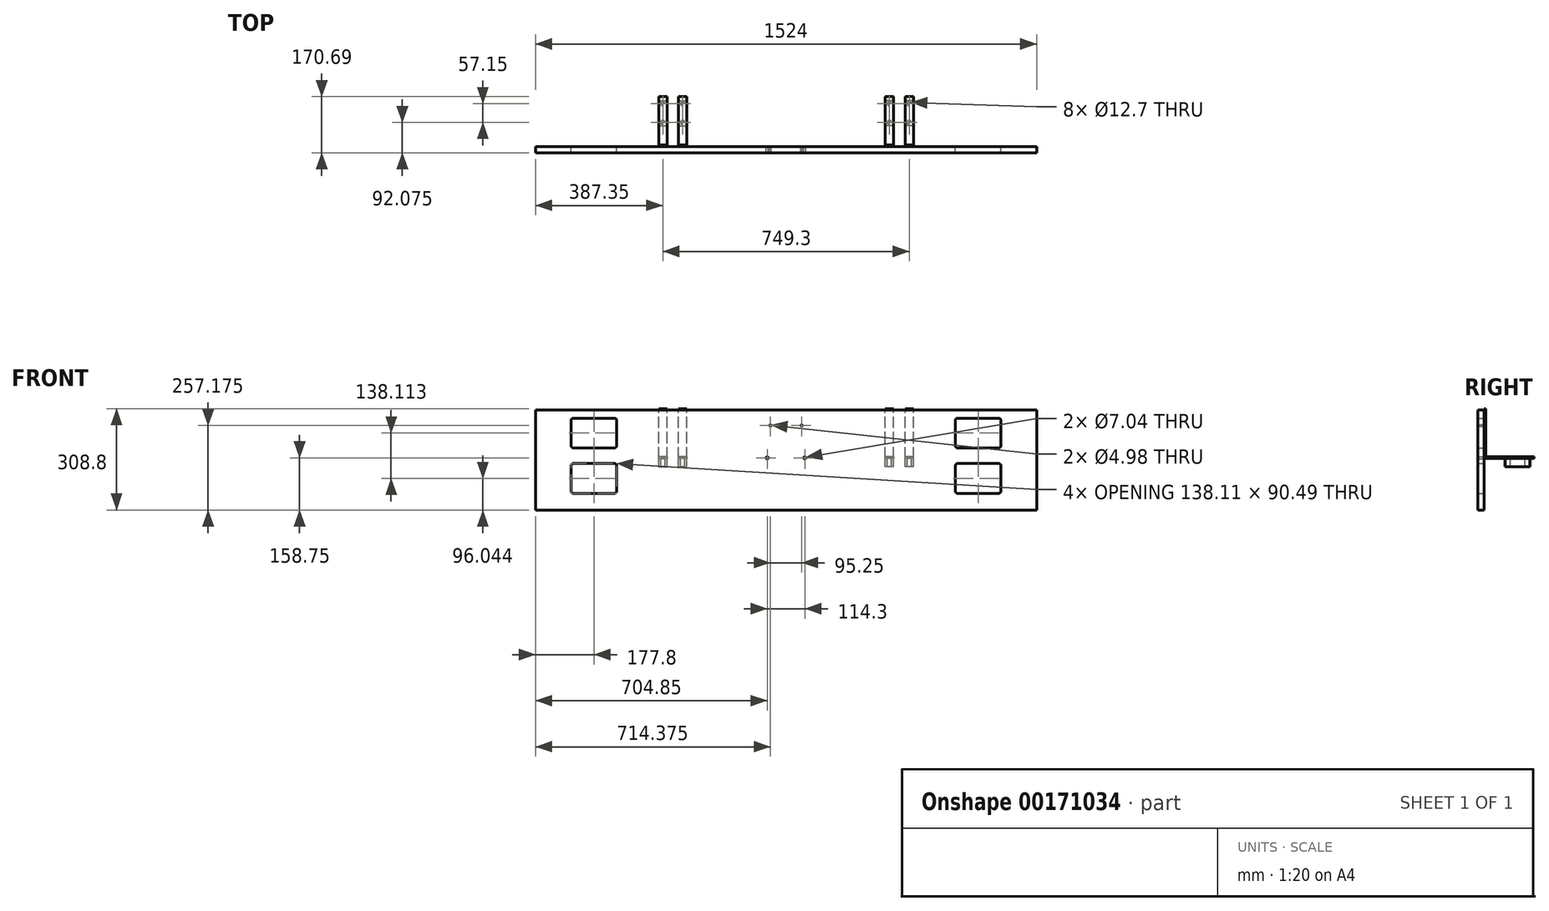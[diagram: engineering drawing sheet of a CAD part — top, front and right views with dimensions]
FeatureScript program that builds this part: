
annotation { "Feature Type Name" : "Feature", "Feature Type Description" : "" }
export const myFeature = defineFeature(function(context is Context, id is Id, definition is map)
    precondition{}
    {
        {
            var Q0;
            Q0=qCreatedBy(makeId("Front.planeOp"),FACE);
            var sketch = newSketch(context, id + "F0", { "sketchPlane" : qUnion([Q0])});
            skLineSegment(sketch, "E0.bottom", {"start": v(-762, 304.8) * mm, "end": v(762, 304.8) * mm});
            skLineSegment(sketch, "E0.top", {"start": v(-762, 0) * mm, "end": v(762, 0) * mm});
            skLineSegment(sketch, "E0.left", {"start": v(-762, 304.8) * mm, "end": v(-762, 0) * mm});
            skLineSegment(sketch, "E0.right", {"start": v(762, 304.8) * mm, "end": v(762, 0) * mm});
            skLineSegment(sketch, "E1.bottom", {"start": v(-646.9, 279.4) * mm, "end": v(-521.5, 279.4) * mm});
            skLineSegment(sketch, "E1.top", {"start": v(-646.9, 188.91) * mm, "end": v(-521.5, 188.91) * mm});
            skLineSegment(sketch, "E1.left", {"start": v(-653.26, 273.05) * mm, "end": v(-653.26, 195.26) * mm});
            skLineSegment(sketch, "E1.right", {"start": v(-515.14, 273.05) * mm, "end": v(-515.14, 195.26) * mm});
            skLineSegment(sketch, "E2.bottom", {"start": v(-646.9, 141.29) * mm, "end": v(-521.5, 141.29) * mm});
            skLineSegment(sketch, "E2.top", {"start": v(-646.9, 50.8) * mm, "end": v(-521.5, 50.8) * mm});
            skLineSegment(sketch, "E2.left", {"start": v(-653.26, 134.94) * mm, "end": v(-653.26, 57.15) * mm});
            skLineSegment(sketch, "E2.right", {"start": v(-515.14, 134.94) * mm, "end": v(-515.14, 57.15) * mm});
            skLineSegment(sketch, "E3", {"start": v(0, 0) * mm, "end": v(0, 112.5) * mm, "construction": true});
            skPoint(sketch, "E4.visualSharp", {"position": v(-515.14, 279.4) * mm});
            skArc(sketch, "E4.filletArc", {"start": v(-515.14, 273.05) * mm, "mid": v(-517, 277.54) * mm, "end": v(-521.5, 279.4) * mm});
            skPoint(sketch, "E5.visualSharp", {"position": v(-653.26, 279.4) * mm});
            skArc(sketch, "E5.filletArc", {"start": v(-646.9, 279.4) * mm, "mid": v(-651.4, 277.54) * mm, "end": v(-653.26, 273.05) * mm});
            skPoint(sketch, "E6.visualSharp", {"position": v(-515.14, 188.91) * mm});
            skArc(sketch, "E6.filletArc", {"start": v(-521.5, 188.91) * mm, "mid": v(-517, 190.77) * mm, "end": v(-515.14, 195.26) * mm});
            skPoint(sketch, "E7.visualSharp", {"position": v(-653.26, 188.91) * mm});
            skArc(sketch, "E7.filletArc", {"start": v(-653.26, 195.26) * mm, "mid": v(-651.4, 190.77) * mm, "end": v(-646.9, 188.91) * mm});
            skPoint(sketch, "E8.visualSharp", {"position": v(-653.26, 50.8) * mm});
            skArc(sketch, "E8.filletArc", {"start": v(-653.26, 57.15) * mm, "mid": v(-651.4, 52.66) * mm, "end": v(-646.9, 50.8) * mm});
            skPoint(sketch, "E9.visualSharp", {"position": v(-515.14, 50.8) * mm});
            skArc(sketch, "E9.filletArc", {"start": v(-521.5, 50.8) * mm, "mid": v(-517, 52.66) * mm, "end": v(-515.14, 57.15) * mm});
            skPoint(sketch, "E10.visualSharp", {"position": v(-515.14, 141.29) * mm});
            skArc(sketch, "E10.filletArc", {"start": v(-515.14, 134.94) * mm, "mid": v(-517, 139.43) * mm, "end": v(-521.5, 141.29) * mm});
            skPoint(sketch, "E11.visualSharp", {"position": v(-653.26, 141.29) * mm});
            skArc(sketch, "E11.filletArc", {"start": v(-646.9, 141.29) * mm, "mid": v(-651.4, 139.43) * mm, "end": v(-653.26, 134.94) * mm});
            skArc(sketch, "E12.MirrorCS", {"start": v(653.26, 195.26) * mm, "mid": v(651.4, 190.77) * mm, "end": v(646.9, 188.91) * mm});
            skArc(sketch, "E13.MirrorCS", {"start": v(521.5, 50.8) * mm, "mid": v(517, 52.66) * mm, "end": v(515.14, 57.15) * mm});
            skArc(sketch, "E14.MirrorCS", {"start": v(646.9, 141.29) * mm, "mid": v(651.4, 139.43) * mm, "end": v(653.26, 134.94) * mm});
            skArc(sketch, "E15.MirrorCS", {"start": v(515.14, 134.94) * mm, "mid": v(517, 139.43) * mm, "end": v(521.5, 141.29) * mm});
            skArc(sketch, "E16.MirrorCS", {"start": v(515.14, 273.05) * mm, "mid": v(517, 277.54) * mm, "end": v(521.5, 279.4) * mm});
            skArc(sketch, "E17.MirrorCS", {"start": v(653.26, 57.15) * mm, "mid": v(651.4, 52.66) * mm, "end": v(646.9, 50.8) * mm});
            skArc(sketch, "E18.MirrorCS", {"start": v(646.9, 279.4) * mm, "mid": v(651.4, 277.54) * mm, "end": v(653.26, 273.05) * mm});
            skArc(sketch, "E19.MirrorCS", {"start": v(521.5, 188.91) * mm, "mid": v(517, 190.77) * mm, "end": v(515.14, 195.26) * mm});
            skPoint(sketch, "E20.MirrorP", {"position": v(515.14, 188.91) * mm});
            skLineSegment(sketch, "E21.MirrorCS", {"start": v(515.14, 134.94) * mm, "end": v(515.14, 57.15) * mm});
            skPoint(sketch, "E22.MirrorP", {"position": v(653.26, 279.4) * mm});
            skLineSegment(sketch, "E23.MirrorCS", {"start": v(653.26, 134.94) * mm, "end": v(653.26, 57.15) * mm});
            skLineSegment(sketch, "E24.MirrorCS", {"start": v(646.9, 50.8) * mm, "end": v(521.5, 50.8) * mm});
            skLineSegment(sketch, "E25.MirrorCS", {"start": v(646.9, 141.29) * mm, "end": v(521.5, 141.29) * mm});
            skPoint(sketch, "E26.MirrorP", {"position": v(515.14, 279.4) * mm});
            skPoint(sketch, "E27.MirrorP", {"position": v(653.26, 188.91) * mm});
            skLineSegment(sketch, "E28.MirrorCS", {"start": v(653.26, 273.05) * mm, "end": v(653.26, 195.26) * mm});
            skLineSegment(sketch, "E29.MirrorCS", {"start": v(646.9, 188.91) * mm, "end": v(521.5, 188.91) * mm});
            skLineSegment(sketch, "E30.MirrorCS", {"start": v(646.9, 279.4) * mm, "end": v(521.5, 279.4) * mm});
            skPoint(sketch, "E31.MirrorP", {"position": v(653.26, 141.29) * mm});
            skPoint(sketch, "E32.MirrorP", {"position": v(653.26, 50.8) * mm});
            skLineSegment(sketch, "E33.MirrorCS", {"start": v(515.14, 273.05) * mm, "end": v(515.14, 195.26) * mm});
            skPoint(sketch, "E34.MirrorP", {"position": v(515.14, 50.8) * mm});
            skPoint(sketch, "E35.MirrorP", {"position": v(515.14, 141.29) * mm});
            skLineSegment(sketch, "E36", {"start": v(-584.2, 279.4) * mm, "end": v(-584.2, -469.9) * mm, "construction": true});
            skLineSegment(sketch, "E37", {"start": v(-584.2, -469.9) * mm, "end": v(584.2, -469.9) * mm, "construction": true});
            skPoint(sketch, "E37.endSnap0", {"position": v(584.2, 50.8) * mm});
            skLineSegment(sketch, "E38", {"start": v(-294.85, -469.9) * mm, "end": v(-294.85, 157.16) * mm, "construction": true});
            skLineSegment(sketch, "E39", {"start": v(0, -469.9) * mm, "end": v(0, 158.75) * mm, "construction": true});
            skLineSegment(sketch, "E40", {"start": v(-57.15, 158.75) * mm, "end": v(57.15, 158.75) * mm, "construction": true});
            skCircle(sketch, "E41", {"center": v(-57.15, 158.75) * mm, "radius": 3.52 * mm});
            skCircle(sketch, "E42", {"center": v(57.15, 158.75) * mm, "radius": 3.52 * mm});
            skCircle(sketch, "E43", {"center": v(-47.63, 257.18) * mm, "radius": 2.49 * mm});
            skCircle(sketch, "E44", {"center": v(47.62, 257.18) * mm, "radius": 2.49 * mm});
            skSolve(sketch);
        }
        {
            var Q0;
            Q0=makeQuery(id+"F0.imprint","IMPRINT",FACE,{"disambiguationData":[TD([[makeQuery(id+"F0.imprint","IMPRINT",EDGE,{"derivedFrom":sQuery(id+"F0.wireOp",EDGE,"E0.bottom")}),-1.0]])]});
            extrude(context, id + "F1", {"entities" : qUnion([Q0]), "depth" : 19.05 * mm});
        }
        {
            var Q0;
            Q0=sQuery(id+"F0.wireOp",EDGE,"E38");
            var Q1;
            Q1=sQuery(id+"F0.wireOp",VERTEX,"E38.end");
            cPlane(context, id + "F2", {"entities" : qUnion([Q0, Q1]), "cplaneType" : CPlaneType.LINE_POINT, "offset" : 25.4 * mm, "width" : 152.4 * mm, "height" : 152.4 * mm});
        }
        {
            var Q0;
            Q0=qCreatedBy(id+"F2.planeOp",FACE);
            var sketch = newSketch(context, id + "F3", { "sketchPlane" : qUnion([Q0])});
            skLineSegment(sketch, "E45", {"start": v(0, -2.13) * mm, "end": v(0, 78.43) * mm, "construction": true});
            skCircle(sketch, "E46", {"center": v(-374.65, 73.02) * mm, "radius": 6.35 * mm});
            skCircle(sketch, "E47", {"center": v(-314.33, 73.02) * mm, "radius": 6.35 * mm});
            skLineSegment(sketch, "E48.bottom", {"start": v(-387.35, 139.7) * mm, "end": v(-361.95, 139.7) * mm});
            skLineSegment(sketch, "E48.top", {"start": v(-387.35, 63.5) * mm, "end": v(-361.95, 63.5) * mm});
            skLineSegment(sketch, "E48.left", {"start": v(-387.35, 139.7) * mm, "end": v(-387.35, 63.5) * mm});
            skLineSegment(sketch, "E48.right", {"start": v(-361.95, 139.7) * mm, "end": v(-361.95, 63.5) * mm});
            skLineSegment(sketch, "E49.bottom", {"start": v(-327.03, 139.7) * mm, "end": v(-301.63, 139.7) * mm});
            skLineSegment(sketch, "E49.top", {"start": v(-327.03, 63.5) * mm, "end": v(-301.63, 63.5) * mm});
            skLineSegment(sketch, "E49.left", {"start": v(-327.03, 139.7) * mm, "end": v(-327.03, 63.5) * mm});
            skLineSegment(sketch, "E49.right", {"start": v(-301.63, 139.7) * mm, "end": v(-301.63, 63.5) * mm});
            skCircle(sketch, "E50", {"center": v(-374.65, 130.17) * mm, "radius": 6.35 * mm});
            skCircle(sketch, "E51", {"center": v(-314.33, 130.17) * mm, "radius": 6.35 * mm});
            skLineSegment(sketch, "E52", {"start": v(-387.35, 101.6) * mm, "end": v(-380.85, 101.6) * mm, "construction": true});
            skLineSegment(sketch, "E53.MirrorCS", {"start": v(387.35, 101.6) * mm, "end": v(380.85, 101.6) * mm, "construction": true});
            skLineSegment(sketch, "E54.MirrorCS", {"start": v(387.35, 63.5) * mm, "end": v(361.95, 63.5) * mm});
            skLineSegment(sketch, "E55.MirrorCS", {"start": v(327.03, 63.5) * mm, "end": v(301.63, 63.5) * mm});
            skCircle(sketch, "E56.MirrorC", {"center": v(374.65, 73.02) * mm, "radius": 6.35 * mm});
            skCircle(sketch, "E57.MirrorC", {"center": v(314.33, 73.02) * mm, "radius": 6.35 * mm});
            skCircle(sketch, "E58.MirrorC", {"center": v(314.33, 130.17) * mm, "radius": 6.35 * mm});
            skCircle(sketch, "E59.MirrorC", {"center": v(374.65, 130.17) * mm, "radius": 6.35 * mm});
            skLineSegment(sketch, "E60.MirrorCS", {"start": v(301.63, 139.7) * mm, "end": v(301.63, 63.5) * mm});
            skLineSegment(sketch, "E61.MirrorCS", {"start": v(327.03, 139.7) * mm, "end": v(327.03, 63.5) * mm});
            skLineSegment(sketch, "E62.MirrorCS", {"start": v(387.35, 139.7) * mm, "end": v(361.95, 139.7) * mm});
            skLineSegment(sketch, "E63.MirrorCS", {"start": v(387.35, 139.7) * mm, "end": v(387.35, 63.5) * mm});
            skLineSegment(sketch, "E64.MirrorCS", {"start": v(361.95, 139.7) * mm, "end": v(361.95, 63.5) * mm});
            skLineSegment(sketch, "E65.MirrorCS", {"start": v(327.03, 139.7) * mm, "end": v(301.63, 139.7) * mm});
            skSolve(sketch);
        }
        {
            var Q0;
            Q0 = qSketchRegion(id + "F3", true);
            extrude(context, id + "F4", {"entities" : qUnion([Q0]), "oppositeDirection" : true, "depth" : 25.4 * mm});
        }
        {
            var Q0;
            Q0=qCreatedBy(makeId("Right.planeOp"),FACE);
            var sketch = newSketch(context, id + "F5", { "sketchPlane" : qUnion([Q0])});
            skLineSegment(sketch, "E66.0", {"start": v(139.7, 157.16) * mm, "end": v(63.5, 157.16) * mm, "construction": true});
            skLineSegment(sketch, "E66.1", {"start": v(0, 304.8) * mm, "end": v(0, 0) * mm, "construction": true});
            skLineSegment(sketch, "E67.bottom", {"start": v(0, 157.16) * mm, "end": v(151.64, 157.16) * mm});
            skLineSegment(sketch, "E67.top", {"start": v(4.83, 161.99) * mm, "end": v(151.64, 161.99) * mm});
            skLineSegment(sketch, "E67.left", {"start": v(0, 157.16) * mm, "end": v(0, 161.99) * mm});
            skLineSegment(sketch, "E67.right", {"start": v(151.64, 157.16) * mm, "end": v(151.64, 161.99) * mm});
            skLineSegment(sketch, "E68.bottom", {"start": v(0, 157.16) * mm, "end": v(4.83, 157.16) * mm});
            skLineSegment(sketch, "E68.top", {"start": v(0, 308.8) * mm, "end": v(4.83, 308.8) * mm});
            skLineSegment(sketch, "E68.left", {"start": v(0, 157.16) * mm, "end": v(0, 308.8) * mm});
            skLineSegment(sketch, "E68.right", {"start": v(4.83, 161.99) * mm, "end": v(4.83, 308.8) * mm});
            skSolve(sketch);
        }
        {
            var Q0;
            Q0 = qSketchRegion(id + "F5", true);
            extrude(context, id + "F6", {"entities" : qUnion([Q0]), "endBound" : BoundingType.SYMMETRIC, "depth" : 774.7 * mm});
        }
        {
            var Q0;
            Q0=makeQuery(id+"F1.opExtrude","CAP_FACE",FACE,{"disambiguationData":[OSD([sQuery(id+"F0.wireOp",EDGE,"E0.bottom"),sQuery(id+"F0.wireOp",EDGE,"E0.top"),sQuery(id+"F0.wireOp",EDGE,"E0.left"),sQuery(id+"F0.wireOp",EDGE,"E0.right"),sQuery(id+"F0.wireOp",EDGE,"E1.bottom"),sQuery(id+"F0.wireOp",EDGE,"E1.top"),sQuery(id+"F0.wireOp",EDGE,"E1.left"),sQuery(id+"F0.wireOp",EDGE,"E1.right"),sQuery(id+"F0.wireOp",EDGE,"E2.bottom"),sQuery(id+"F0.wireOp",EDGE,"E2.top"),sQuery(id+"F0.wireOp",EDGE,"E2.left"),sQuery(id+"F0.wireOp",EDGE,"E2.right"),sQuery(id+"F0.wireOp",EDGE,"E4.filletArc"),sQuery(id+"F0.wireOp",EDGE,"E5.filletArc"),sQuery(id+"F0.wireOp",EDGE,"E6.filletArc"),sQuery(id+"F0.wireOp",EDGE,"E7.filletArc"),sQuery(id+"F0.wireOp",EDGE,"E8.filletArc"),sQuery(id+"F0.wireOp",EDGE,"E9.filletArc"),sQuery(id+"F0.wireOp",EDGE,"E10.filletArc"),sQuery(id+"F0.wireOp",EDGE,"E11.filletArc"),sQuery(id+"F0.wireOp",EDGE,"E12.MirrorCS"),sQuery(id+"F0.wireOp",EDGE,"E13.MirrorCS"),sQuery(id+"F0.wireOp",EDGE,"E14.MirrorCS"),sQuery(id+"F0.wireOp",EDGE,"E15.MirrorCS"),sQuery(id+"F0.wireOp",EDGE,"E16.MirrorCS"),sQuery(id+"F0.wireOp",EDGE,"E17.MirrorCS"),sQuery(id+"F0.wireOp",EDGE,"E18.MirrorCS"),sQuery(id+"F0.wireOp",EDGE,"E19.MirrorCS"),sQuery(id+"F0.wireOp",EDGE,"E21.MirrorCS"),sQuery(id+"F0.wireOp",EDGE,"E23.MirrorCS"),sQuery(id+"F0.wireOp",EDGE,"E24.MirrorCS"),sQuery(id+"F0.wireOp",EDGE,"E25.MirrorCS"),sQuery(id+"F0.wireOp",EDGE,"E28.MirrorCS"),sQuery(id+"F0.wireOp",EDGE,"E29.MirrorCS"),sQuery(id+"F0.wireOp",EDGE,"E30.MirrorCS"),sQuery(id+"F0.wireOp",EDGE,"E33.MirrorCS"),sQuery(id+"F0.wireOp",EDGE,"E41"),sQuery(id+"F0.wireOp",EDGE,"E42"),sQuery(id+"F0.wireOp",EDGE,"E43"),sQuery(id+"F0.wireOp",EDGE,"E44")])],"isStart":true});
            var sketch = newSketch(context, id + "F7", { "sketchPlane" : qUnion([Q0])});
            skLineSegment(sketch, "E69.0", {"start": v(-361.95, 131.76) * mm, "end": v(-361.95, 157.16) * mm, "construction": true});
            skLineSegment(sketch, "E69.1", {"start": v(-327.03, 131.76) * mm, "end": v(-327.03, 157.16) * mm, "construction": true});
            skLineSegment(sketch, "E69.2", {"start": v(-301.63, 131.76) * mm, "end": v(-301.63, 157.16) * mm, "construction": true});
            skLineSegment(sketch, "E69.3", {"start": v(327.03, 131.76) * mm, "end": v(327.03, 157.16) * mm, "construction": true});
            skLineSegment(sketch, "E69.4", {"start": v(361.95, 131.76) * mm, "end": v(361.95, 157.16) * mm, "construction": true});
            skLineSegment(sketch, "E69.5", {"start": v(301.63, 131.76) * mm, "end": v(301.63, 157.16) * mm, "construction": true});
            skLineSegment(sketch, "E70.bottom", {"start": v(327.03, 157.16) * mm, "end": v(361.95, 157.16) * mm});
            skLineSegment(sketch, "E70.top", {"start": v(327.03, 313.57) * mm, "end": v(361.95, 313.57) * mm});
            skLineSegment(sketch, "E70.left", {"start": v(327.03, 157.16) * mm, "end": v(327.03, 313.57) * mm});
            skLineSegment(sketch, "E70.right", {"start": v(361.95, 157.16) * mm, "end": v(361.95, 313.57) * mm});
            skLineSegment(sketch, "E71.bottom", {"start": v(301.63, 157.16) * mm, "end": v(-301.63, 157.16) * mm});
            skLineSegment(sketch, "E71.top", {"start": v(301.63, 326.16) * mm, "end": v(-301.63, 326.16) * mm});
            skLineSegment(sketch, "E71.left", {"start": v(301.63, 157.16) * mm, "end": v(301.63, 326.16) * mm});
            skLineSegment(sketch, "E71.right", {"start": v(-301.63, 157.16) * mm, "end": v(-301.63, 326.16) * mm});
            skLineSegment(sketch, "E72.bottom", {"start": v(-327.03, 157.16) * mm, "end": v(-361.95, 157.16) * mm});
            skLineSegment(sketch, "E72.top", {"start": v(-327.03, 329.6) * mm, "end": v(-361.95, 329.6) * mm});
            skLineSegment(sketch, "E72.left", {"start": v(-327.03, 157.16) * mm, "end": v(-327.03, 329.6) * mm});
            skLineSegment(sketch, "E72.right", {"start": v(-361.95, 157.16) * mm, "end": v(-361.95, 329.6) * mm});
            skSolve(sketch);
        }
        {
            var Q0;
            Q0 = qSketchRegion(id + "F7", true);
            var Q1;
            Q1=makeQuery(id+"F6.opExtrude","SWEPT_FACE",FACE,{"disambiguationData":[OSD([sQuery(id+"F5.wireOp",EDGE,"E67.right")])]});
            extrude(context, id + "F8", {"entities" : qUnion([Q0]), "operationType" : NewBodyOperationType.REMOVE, "endBound" : BoundingType.UP_TO_SURFACE, "endBoundEntityFace" : qUnion([Q1]), "depth" : 25.4 * mm});
        }
    });
